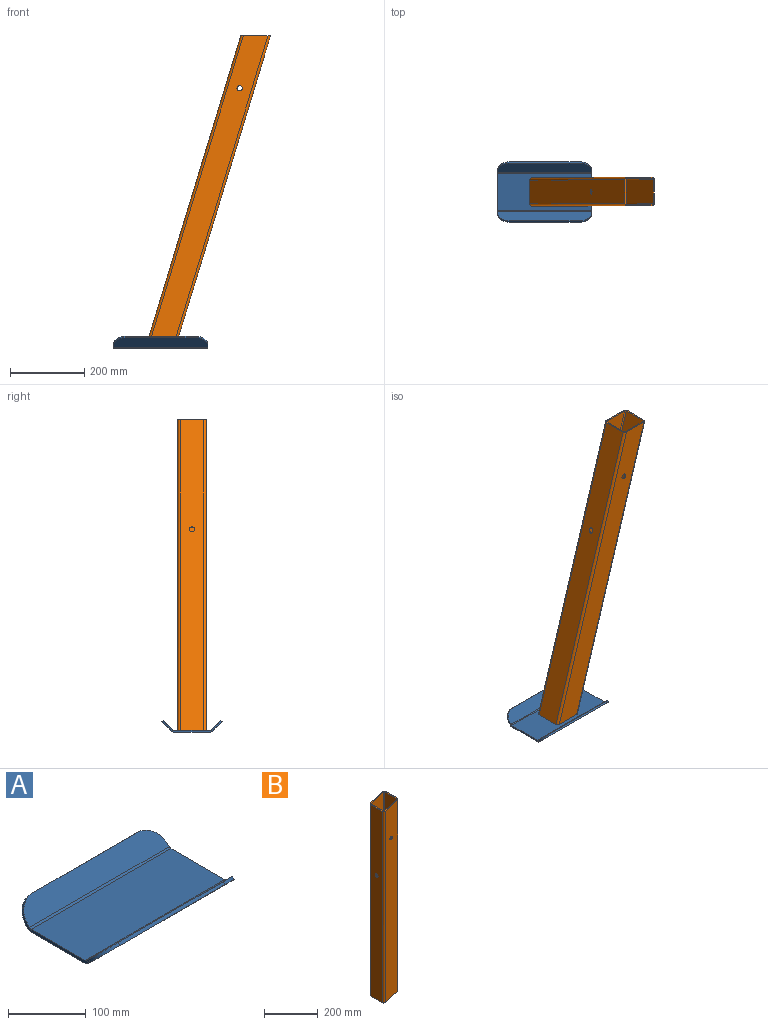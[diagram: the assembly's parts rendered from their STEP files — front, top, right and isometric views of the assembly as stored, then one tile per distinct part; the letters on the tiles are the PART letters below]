
ASSEMBLY  parts=2 mates=1
PART A: 26 faces, bbox 254x162x31.6 mm
  f0: plane 97.65x4.55mm, normal (-1,0,0), area 444mm2, adj f2,f3,f12,f23
  f1: plane 97.65x4.55mm, normal (1,0,0), area 444mm2, adj f2,f3,f11,f22
  f2: plane 254x97.65mm, normal (0,0,-1), area 24804.3mm2, adj f0,f1,f13,f24
  f3: plane 254x97.65mm, normal (0,0,1), area 24804.3mm2, adj f0,f1,f14,f25
  f4: plane 6.38x6.38mm, normal (-1,0,0), area 20.3mm2, adj f7,f8,f9,f12
  f5: plane 190.5x3.22mm, normal (0,0.71,0.71), area 866.1mm2, adj f7,f8,f9,f10
  f6: plane 6.38x6.38mm, normal (1,0,0), area 20.3mm2, adj f7,f8,f10,f11
  f7: plane 254x25.61mm, normal (0,0.71,-0.71), area 8767.6mm2, adj f4,f5,f6,f9,f10,f13
  f8: plane 254x25.61mm, normal (0,-0.71,0.71), area 8767.6mm2, adj f4,f5,f6,f9,f10,f14
  f9: cylinder r=31.75mm len=31.75mm, axis (0,-0.71,0.71), area 226.8mm2, adj f4,f5,f7,f8
  f10: cylinder r=31.75mm len=31.75mm, axis (0,0.71,-0.71), area 226.8mm2, adj f5,f6,f7,f8
  f11: plane 6.58x5.94mm, normal (1,0,0), area 25.1mm2, adj f1,f6,f13,f14
  f12: plane 6.58x5.94mm, normal (-1,0,0), area 25.1mm2, adj f0,f4,f13,f14
  f13: cylinder r=9.31mm len=254mm, axis (1,0,0), area 1857.1mm2, adj f2,f7,f11,f12
  f14: cylinder r=4.76mm len=254mm, axis (1,0,0), area 950.1mm2, adj f3,f8,f11,f12
  f15: plane 6.38x6.38mm, normal (-1,0,0), area 20.3mm2, adj f18,f19,f21,f23
  f16: plane 6.38x6.38mm, normal (1,0,0), area 20.3mm2, adj f18,f19,f20,f22
  f17: plane 190.5x3.22mm, normal (0,-0.71,0.71), area 866.1mm2, adj f18,f19,f20,f21
  f18: plane 254x25.61mm, normal (0,-0.71,-0.71), area 8767.6mm2, adj f15,f16,f17,f20,f21,f24
  f19: plane 254x25.61mm, normal (0,0.71,0.71), area 8767.6mm2, adj f15,f16,f17,f20,f21,f25
  f20: cylinder r=31.75mm len=31.75mm, axis (0,-0.71,-0.71), area 226.8mm2, adj f16,f17,f18,f19
  f21: cylinder r=31.75mm len=31.75mm, axis (0,0.71,0.71), area 226.8mm2, adj f15,f17,f18,f19
  f22: plane 6.58x5.94mm, normal (1,0,0), area 25.1mm2, adj f1,f16,f24,f25
  f23: plane 6.58x5.94mm, normal (-1,0,0), area 25.1mm2, adj f0,f15,f24,f25
  f24: cylinder r=9.31mm len=254mm, axis (1,0,0), area 1857.1mm2, adj f2,f18,f22,f23
  f25: cylinder r=4.76mm len=254mm, axis (1,0,0), area 950.1mm2, adj f3,f19,f22,f23
PART B: 22 faces, bbox 76.2x76.2x897.1 mm
  f0: cylinder r=3.3mm len=874.76mm, axis (0,0,-1), area 4532mm2, adj f1,f7,f8,f9
  f1: plane 873.76x63.5mm, normal (-1,0,0), area 55322.8mm2, adj f0,f2,f8,f9,f21
  f2: cylinder r=3.3mm len=874.76mm, axis (0,0,-1), area 4532mm2, adj f1,f3,f8,f9
  f3: plane 893.17x63.5mm, normal (0,1,0), area 55322.8mm2, adj f2,f4,f8,f9,f11
  f4: cylinder r=3.3mm len=874.76mm, axis (0,0,-1), area 4532mm2, adj f3,f5,f8,f9
  f5: plane 873.76x63.5mm, normal (1,0,0), area 55322.8mm2, adj f4,f6,f8,f9,f20
  f6: cylinder r=3.3mm len=874.76mm, axis (0,0,-1), area 4532mm2, adj f5,f7,f8,f9
  f7: plane 893.17x63.5mm, normal (0,-1,0), area 55322.8mm2, adj f0,f6,f8,f9,f10
  f8: plane 76.2x76.2mm, normal (0.29,0,-0.96), area 906.2mm2, adj f0,f1,f2,f3,f4,f5,f6,f7
  f9: plane 76.2x76.2mm, normal (-0.29,0,0.96), area 906.2mm2, adj f0,f1,f2,f3,f4,f5,f6,f7
  f10: cylinder r=7.15mm len=14.3mm, axis (0,-1,0), area 136.9mm2, adj f7,f17
  f11: cylinder r=7.15mm len=14.3mm, axis (0,-1,0), area 136.9mm2, adj f3,f13
  f12: cylinder r=6.35mm len=875.7mm, axis (0,0,-1), area 8715.3mm2, adj f8,f9,f13,f18
  f13: plane 893.17x63.5mm, normal (0,-1,0), area 55322.8mm2, adj f8,f9,f11,f12,f14
  f14: cylinder r=6.35mm len=875.7mm, axis (0,0,-1), area 8715.3mm2, adj f8,f9,f13,f19
  f15: cylinder r=6.35mm len=875.7mm, axis (0,0,-1), area 8715.3mm2, adj f8,f9,f17,f18
  f16: cylinder r=6.35mm len=875.7mm, axis (0,0,-1), area 8715.3mm2, adj f8,f9,f17,f19
  f17: plane 893.17x63.5mm, normal (0,1,0), area 55322.8mm2, adj f8,f9,f10,f15,f16
  f18: plane 873.76x63.5mm, normal (1,0,0), area 55322.8mm2, adj f8,f9,f12,f15,f21
  f19: plane 873.76x63.5mm, normal (-1,0,0), area 55322.8mm2, adj f8,f9,f14,f16,f20
  f20: cylinder r=7.15mm len=14.3mm, axis (1,0,0), area 136.9mm2, adj f5,f19
  f21: cylinder r=7.15mm len=14.3mm, axis (1,0,0), area 136.9mm2, adj f1,f18
PLACE A t=(-244.58,-8.17,109.84)mm
PLACE B rot(axis=(0,1,0),17deg) t=(-243.85,-8.17,527.63)mm
MATE planar B.f8 <-> A.f3  axis (0,0,-1) through (-371.58,-46.27,109.84)mm
